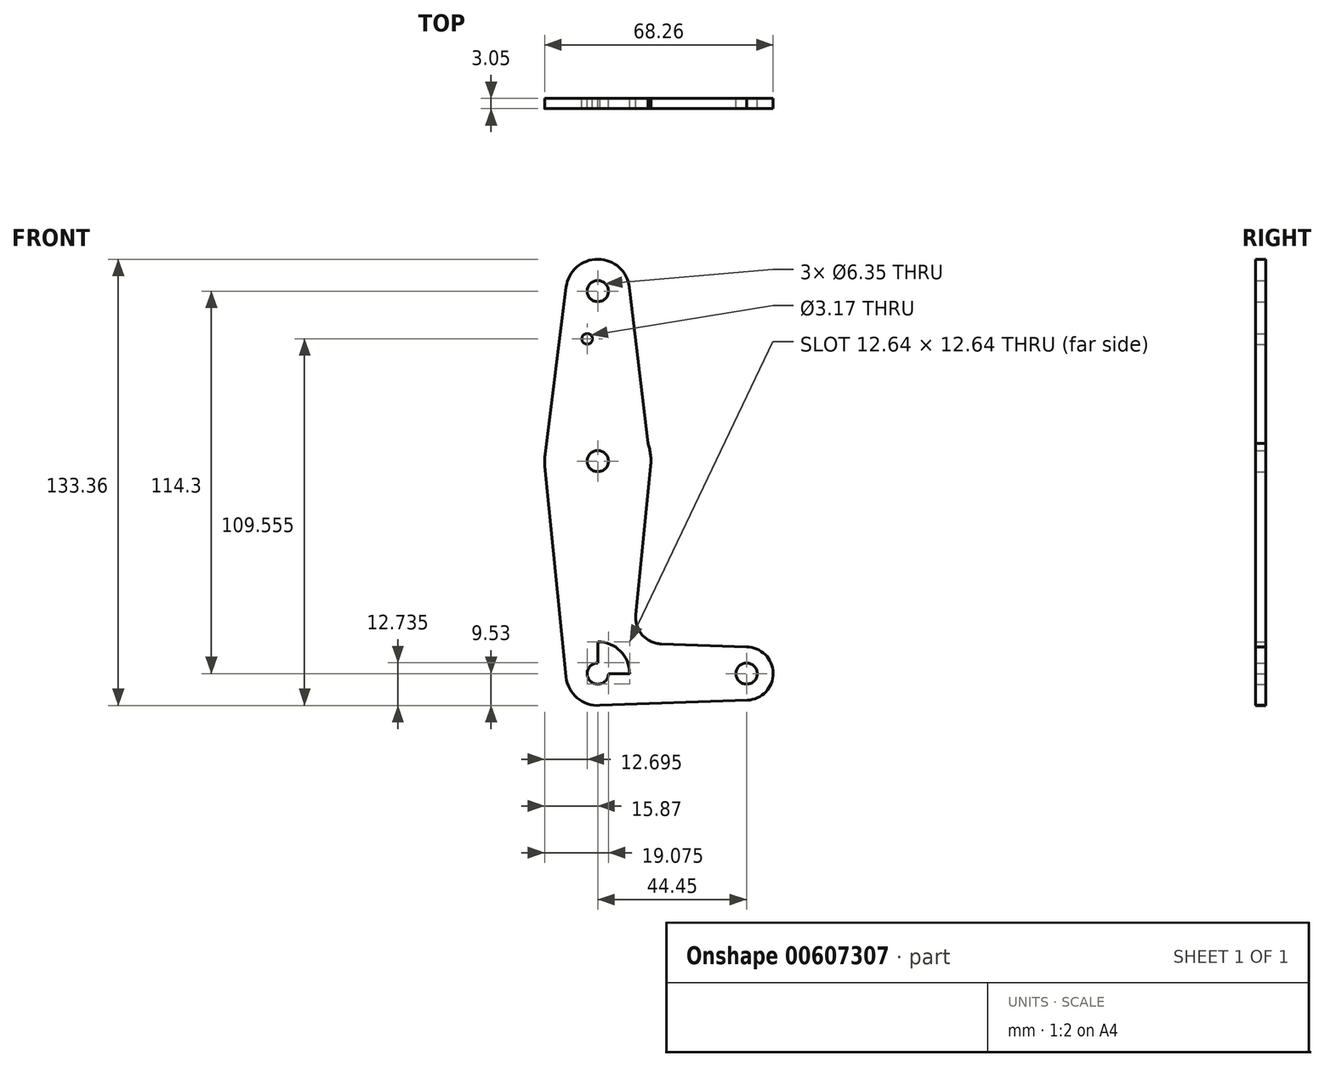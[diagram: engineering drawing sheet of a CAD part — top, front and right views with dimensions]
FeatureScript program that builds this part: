
annotation { "Feature Type Name" : "Feature", "Feature Type Description" : "" }
export const myFeature = defineFeature(function(context is Context, id is Id, definition is map)
    precondition{}
    {
        {
            var Q0;
            Q0=qCreatedBy(makeId("Front.planeOp"),FACE);
            var sketch = newSketch(context, id + "F0", { "sketchPlane" : qUnion([Q0])});
            skLineSegment(sketch, "E0", {"start": v(0, 0) * mm, "end": v(44.45, 0) * mm});
            skCircle(sketch, "E1", {"center": v(44.45, 0) * mm, "radius": 7.94 * mm});
            skCircle(sketch, "E2", {"center": v(0, 63.5) * mm, "radius": 15.88 * mm});
            skCircle(sketch, "E3", {"center": v(0, 114.3) * mm, "radius": 9.53 * mm});
            skLineSegment(sketch, "E4", {"start": v(0, 0) * mm, "end": v(0, 114.3) * mm});
            skLineSegment(sketch, "E5", {"start": v(-9.45, 115.5) * mm, "end": v(-15.75, 65.48) * mm});
            skLineSegment(sketch, "E6", {"start": v(9.46, 115.42) * mm, "end": v(15.8, 61.91) * mm});
            skLineSegment(sketch, "E7", {"start": v(0, -9.52) * mm, "end": v(44.73, -7.93) * mm});
            skCircle(sketch, "E8", {"center": v(0, 0) * mm, "radius": 9.53 * mm});
            skLineSegment(sketch, "E9", {"start": v(44.45, 7.94) * mm, "end": v(18.97, 8.85) * mm});
            skLineSegment(sketch, "E10", {"start": v(15.8, 61.91) * mm, "end": v(11.34, 17.6) * mm});
            skPoint(sketch, "E11.newPointA", {"position": v(9.57, 0) * mm});
            skPoint(sketch, "E11.newPointB", {"position": v(0, 9.53) * mm});
            skArc(sketch, "E11.filletArc", {"start": v(11.34, 17.6) * mm, "mid": v(13.26, 11.57) * mm, "end": v(18.97, 8.85) * mm});
            skCircle(sketch, "E12", {"center": v(0, 63.5) * mm, "radius": 3.18 * mm});
            skCircle(sketch, "E13", {"center": v(0, 114.3) * mm, "radius": 3.18 * mm});
            skCircle(sketch, "E14", {"center": v(-3.18, 100.03) * mm, "radius": 1.59 * mm});
            skCircle(sketch, "E15", {"center": v(0, 0) * mm, "radius": 3.18 * mm});
            skCircle(sketch, "E16", {"center": v(44.45, 0) * mm, "radius": 3.18 * mm});
            skLineSegment(sketch, "E17", {"start": v(-15.8, 61.91) * mm, "end": v(-9.48, -0.95) * mm});
            skSolve(sketch);
        }
        {
            var Q0;
            Q0 = qSketchRegion(id + "F0", true);
            extrude(context, id + "F1", {"entities" : qUnion([Q0]), "depth" : 3.05 * mm, "offsetDistance" : 25.4 * mm});
        }
    });
